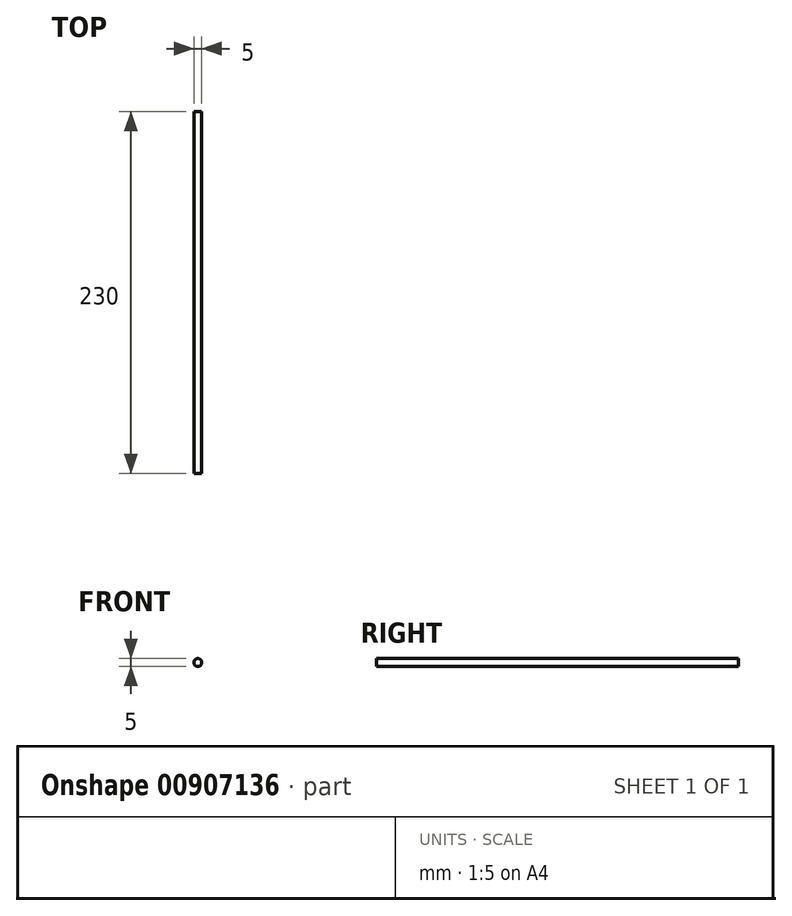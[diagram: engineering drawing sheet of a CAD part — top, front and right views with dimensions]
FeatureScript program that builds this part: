
annotation { "Feature Type Name" : "Feature", "Feature Type Description" : "" }
export const myFeature = defineFeature(function(context is Context, id is Id, definition is map)
    precondition{}
    {
        {
            var Q0;
            Q0=qCreatedBy(makeId("Front.planeOp"),FACE);
            var sketch = newSketch(context, id + "F0", { "sketchPlane" : qUnion([Q0])});
            skCircle(sketch, "E0", {"center": v(0, 0) * mm, "radius": 2.5 * mm});
            skSolve(sketch);
        }
        {
            var Q0;
            Q0=qSketchRegion(id+"F0",true);
            extrude(context, id + "F1", {"entities" : qUnion([Q0]), "endBound" : BoundingType.SYMMETRIC, "depth" : 230 * mm, "offsetDistance" : 25 * mm});
        }
    });
